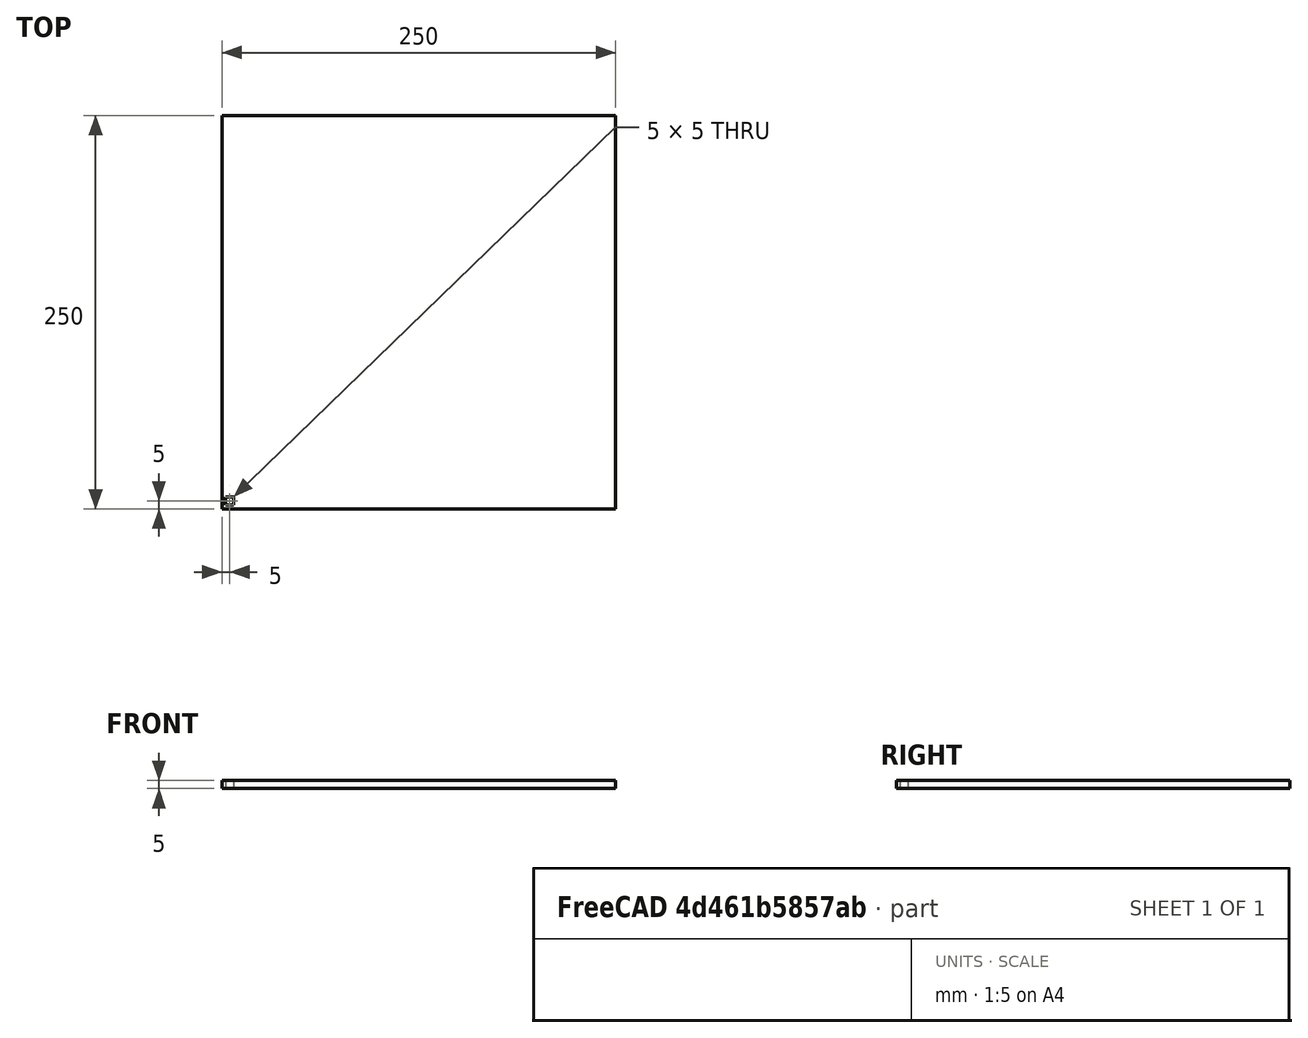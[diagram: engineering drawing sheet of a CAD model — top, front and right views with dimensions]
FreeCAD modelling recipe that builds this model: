
FCSTD DOCUMENT  (FreeCAD 0.18.4R)
Label: floor-v1
License: All rights reserved
LicenseURL: http://en.wikipedia.org/wiki/All_rights_reserved
objects: PartDesign::LinearPattern×2, Part::Box×1, PartDesign::FeatureBase×1, Sketcher::SketchObject×1, PartDesign::Pocket×1, PartDesign::Body×1, PartDesign::MultiTransform×1
note: 9 computed .brp shape members not serialized (recipe doc carries the construction recipe); baked Part::Feature solids carry a one-line shape summary decoded from their .brp

FEATURE [Part::Box] Box  label="Cube"
  AttacherType = Attacher::AttachEngine3D
  Height = 5
  Length = 250
  Width = 250
FEATURE [PartDesign::FeatureBase] BaseFeature
  BaseFeature = -> Box
FEATURE [Sketcher::SketchObject] Sketch
  MapMode = 5
  Placement = pos=(0,0,5) rot=(0,0,1;0rad)
  Support = -> [BaseFeature]
  sketch-geometry (4):
    g0: LineSegment StartX=2.5 StartY=2.5 StartZ=0 EndX=7.5 EndY=2.5 EndZ=0
    g1: LineSegment StartX=7.5 StartY=2.5 StartZ=0 EndX=7.5 EndY=7.5 EndZ=0
    g2: LineSegment StartX=7.5 StartY=7.5 StartZ=0 EndX=2.5 EndY=7.5 EndZ=0
    g3: LineSegment StartX=2.5 StartY=7.5 StartZ=0 EndX=2.5 EndY=2.5 EndZ=0
  constraints (12):
    c: Coincident(g0,g1)
    c: Coincident(g1,g2)
    c: Coincident(g2,g3)
    c: Coincident(g3,g0)
    c: Horizontal(g0)
    c: Horizontal(g2)
    c: Vertical(g1)
    c: Vertical(g3)
    c: DistanceX(g2,g2) = 5
    c: DistanceY(g1,g1) = 5
    c: DistanceX(g-1,g0) = 2.5
    c: DistanceY(g-1,g0) = 2.5
FEATURE [PartDesign::Pocket] Pocket
  BaseFeature = -> BaseFeature
  Length = 5
  Length2 = 100
  Profile = -> Sketch
  Type = 0
FEATURE [PartDesign::LinearPattern] LinearPattern
  Direction = -> Sketch [H_Axis]
  Length = 240
  Occurrences = 25
FEATURE [PartDesign::Body] Body
  BaseFeature = -> Box
  Group = -> [BaseFeature,Sketch,Pocket,MultiTransform,LinearPattern,LinearPattern001]
  Origin = -> Origin
  Tip = -> MultiTransform
FEATURE [PartDesign::MultiTransform] MultiTransform
  BaseFeature = -> Pocket
  Originals = -> [Pocket]
  Transformations = -> [LinearPattern,LinearPattern001]
FEATURE [PartDesign::LinearPattern] LinearPattern001
  Direction = -> MultiTransform [Vertex1336]
  Length = 240
  Occurrences = 25
